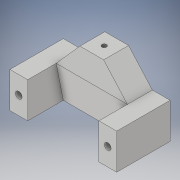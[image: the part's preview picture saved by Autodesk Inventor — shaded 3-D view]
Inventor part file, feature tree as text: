
AUTODESK INVENTOR PART (.ipt)
format: ipt  version: 2019 (Build 230136000, 136)  size: 178,176 bytes
history: native  units: in
note: dims shown in document units (in); Inventor stores cm internally (conversion verified against a paired STEP export)
features: sketch x7, extrude x4, hole x3, projected_geometry x1
ambient origin geometry x8: Origin, YZ Plane, XZ Plane, XY Plane, X Axis, Y Axis, Z Axis, Center Point
bodies: Solid1 (feature_tree)
feature tree (15):
  extrude  "Extrusion1"  Depth=1.5in
  extrude  "Extrusion2"  Depth=0.5in
  hole  "Hole1"  [1 undecoded]
  hole  "Hole2"  [1 undecoded]
  extrude  "Extrusion3"  Depth=0.5in
  extrude  "Extrusion4"  Depth=1.0in
  hole  "Hole3"  [1 undecoded]
  sketch  "Sketch1"  dims[d0=1.5in d1=1.5in]
  sketch  "Sketch2"  dims[d2=0.5in d3=0.5in]
  sketch  "Sketch3"  dims[d5=2.0in d6=0.5in]
  sketch  "Sketch4"  dims[d7=1.0in d8=0.0in d9=0.2in]
  sketch  "Sketch5"  dims[d10=2.0in d11=0.0in d12=0.5in]
  sketch  "Sketch6"  dims[d13=1.0in d14=0.25in]
  projected_geometry  "Projected Loop1"
  sketch  "Sketch7"  dims[d15=0.5in d16=0.5in d17=1.0in d18=0.5in d19=0.25in d20=0.1875in d21=0.75in d22=0.279in d23=0.25in d24=0.5635in d25=1.0in d26=0.8108in d27=1.5in d28=0.8in d29=3.0in d30=1.5in d31=0.35in d32=0.104in d33=0.276in d34=0.279in d35=0.25in d36=0.5635in d37=0.432in d38=0.8108in d39=0.5in d40=0.5in d41=0.75in d42=0.0in d43=2.0in d44=0.6667in d45=0.6667in d46=0.75in d47=0.0in d48=0.13in d49=0.328in d50=0.375in d51=0.25in d52=0.5635in d53=0.484in d54=0.8108in]
note: 3 required parameter values undecoded (feature->parameter linkage not recoverable at this tier; creation-order binding heuristic only, values carry confidence <= 0.55)
